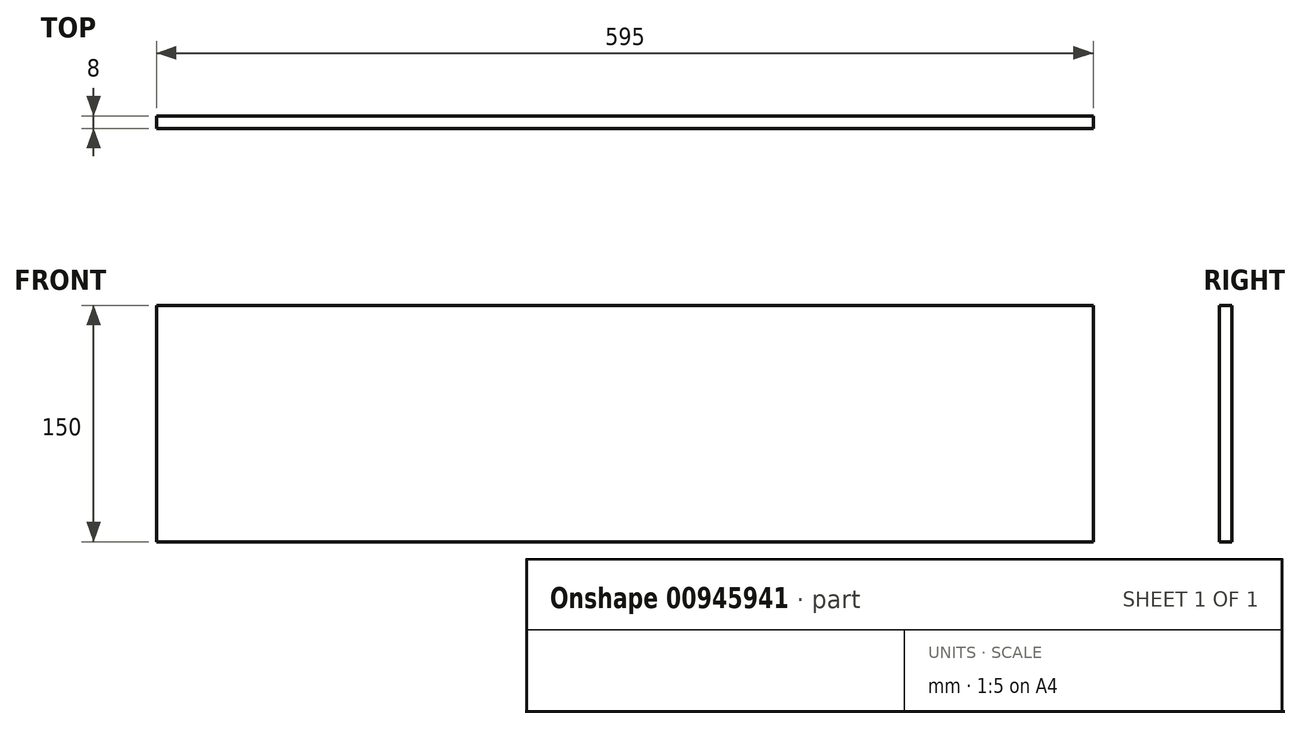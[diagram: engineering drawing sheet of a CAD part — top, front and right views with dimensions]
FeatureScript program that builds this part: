
annotation { "Feature Type Name" : "Feature", "Feature Type Description" : "" }
export const myFeature = defineFeature(function(context is Context, id is Id, definition is map)
    precondition{}
    {
        {
            var Q0;
            Q0=qCreatedBy(makeId("Front.planeOp"),FACE);
            var sketch = newSketch(context, id + "F0", { "sketchPlane" : qUnion([Q0])});
            skLineSegment(sketch, "E0.bottom", {"start": v(297.5, -75) * mm, "end": v(-297.5, -75) * mm});
            skLineSegment(sketch, "E0.top", {"start": v(297.5, 75) * mm, "end": v(-297.5, 75) * mm});
            skLineSegment(sketch, "E0.left", {"start": v(297.5, -75) * mm, "end": v(297.5, 75) * mm});
            skLineSegment(sketch, "E0.right", {"start": v(-297.5, -75) * mm, "end": v(-297.5, 75) * mm});
            skPoint(sketch, "E0.middle", {"position": v(0, 0) * mm});
            skSolve(sketch);
        }
        {
            var Q0;
            Q0 = qSketchRegion(id + "F0", true);
            extrude(context, id + "F1", {"entities" : qUnion([Q0]), "depth" : 8 * mm, "offsetDistance" : 25 * mm});
        }
    });
